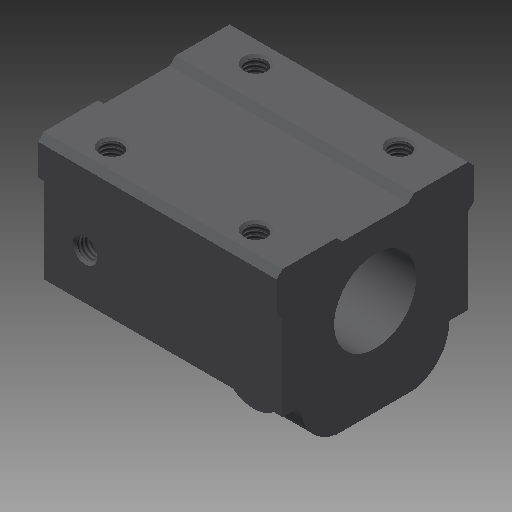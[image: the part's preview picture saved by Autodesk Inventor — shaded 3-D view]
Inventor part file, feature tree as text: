
AUTODESK INVENTOR PART (.ipt)
format: ipt  version: 2018 (Build 220112000, 112)  size: 224,256 bytes
history: native  units: mm
features: sketch x9, other x7, extrude x5, revolve x2, hole x2, pattern_linear x1
ambient origin geometry x8: Origin, YZ Plane, XZ Plane, XY Plane, X Axis, Y Axis, Z Axis, Center Point
bodies: Solid1 (feature_tree)
feature tree (26):
  extrude  "Extrusion1"  Depth=58.0mm TaperAngle=0.0deg
  extrude  "Extrusion2"  TaperAngle=360.0deg  [1 undecoded]
  extrude  "Extrusion3"  Depth=0.8mm TaperAngle=0.0deg
  revolve  "Revolution1"  [1 undecoded]
  revolve  "Revolution2"  [1 undecoded]
  extrude  "Extrusion4"  [1 undecoded]
  extrude  "Extrusion5"  [1 undecoded]
  hole  "Hole1"  [1 undecoded]
  hole  "Hole2"  [1 undecoded]
  pattern_linear  "Rectangular Pattern1"  [2 undecoded]
  other  "bnt_nut_1_XY"
  other  "bnt_nut_1_YZ"
  other  "bnt_nut_1_ZX"
  other  "bnt_nut_1_X"
  other  "bnt_nut_1_Y"
  other  "bnt_nut_1_Z"
  other  "bnt_nut_1_Center"
  sketch  "Sketch_1"  dims[d0=58.0mm d1=0.0mm d2=58.0mm d3=0.0mm]
  sketch  "Sketch_2"  dims[d4=4.6mm d5=0.0mm d6=360.0deg]
  sketch  "Sketch_3"  dims[d7=360.0deg d8=0.8mm d9=0.0mm]
  sketch  "Sketch_4"  dims[d10=0.8mm d11=0.0mm]
  sketch  "Sketch_5"  dims[d12=4.917mm d13=10.5415mm d14=6.0mm d15=2.0mm d16=90.0deg d17=14.140584mm d18=120.0deg]
  sketch  "Sketch_6"  dims[d19=4.917mm d20=10.5415mm d21=6.0mm d22=2.0mm d23=90.0deg d24=13.140584mm d25=120.0deg d26=20.0mm d28=35.0mm d29=20.0mm d31=35.0mm]
  sketch  "Sketch_7"  dims[d32=0.0mm]
  sketch  "Sketch8"
  sketch  "Sketch9"
note: 9 required parameter values undecoded (feature->parameter linkage not recoverable at this tier; creation-order binding heuristic only, values carry confidence <= 0.55)